# Revit family: Sink-Kitchen-KOHLER-Prolific-K-23651_1
name_source: partatom
category: Plumbing Fixtures
revit_build: Autodesk Revit 2015 (Build: 20140606_1530(x64)
units: mm (PartAtom-declared; Revit-internal decimal feet)

## types (1)
- NA-Stainless Steel
    ADA Compliant = No
    Assembly Code = D2010400
    CW Connection = No
    Cold Water Inlet = Cold Water Inlet
    Date Modified = 01/30/2019
    Default Elevation = 36"
    Description = 29 inch x 17-3/4 inch x 10-15/16 inch under-mount single-bowl kitchen sink with accessories
    Drain Included = No
    Finish = Kohler-Metal-NA-Stainless
    HW Connection = No
    Height = 10 15/16"
    Hot Water Inlet = Hot Water Inlet
    Length = 29"
    Manufacturer = KOHLER Co.
    MasterFormat 1995 = 15410
    MasterFormat 2004 = 22.41.16
    Material = 18-Gauge Stainless Steel
    Model = K-23651-NA
    Product Documentation Link = https://www.us.kohler.com
    Product Name = Prolific
    Product Page URL = http://www.us.kohler.com
    URL = https://www.us.kohler.com
    Vent Connection = No
    Waste Connection = Yes
    Waste Water Outlet = Waste Water Outlet
    WaterSense Certified = No
    Width = 17 3/4"

## geometry (parser evidence)
native form markers: Sweep x12
no freeform markers — native parametric forms only
